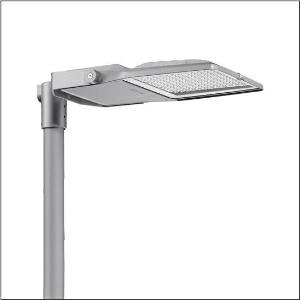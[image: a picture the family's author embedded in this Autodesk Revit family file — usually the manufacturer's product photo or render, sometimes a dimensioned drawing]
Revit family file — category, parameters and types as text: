
# Revit family: floodlight_fl_21_iq_midi___pl52_5xa7781f2d3a_fab9
name_source: partatom
category: Lighting Fixtures
units: mm (PartAtom-declared; Revit-internal decimal feet)

## family parameters
Cut with Voids When Loaded = No
Host = Face
Light Source = No
Part Type = Normal
Room Calculation Point = No
Round Connector Dimension = Use Diameter
Shared = No

## types (1)
- --- (1 x LED, 35760 lm, 270.2 W, 3000K)
    Apparent Load = 270 VA
    CIE Flux Codes = 26 60 98 100 100
    Color Rendering = 70
    Color Temperature = 3000K
    Default Elevation = 1800 mm
    Description = Floodlight FL 21 iQ midi, floodlight, primary light control with lens, of PMMA, primary optical cover: protective disc, of toughened safety glass, transparent, light distribution: PL52, light emission: direct distribution, installation type: surface-mounted, LED, High Power LED, rated luminous flux: 35.760lm, luminous efficacy: 132lm/W, light colour: 730, colour temperature: 3000K, control gear: ECG iQ, control: optimised constant luminous flux control (CLO 2.0), Desk-Remote (wireless, voltage-free reading and setting of iQ features in the workshop via application-optimized NFC function/RFID function), Light-Fading, Smart-Wire, Night-Set, Lumen-Switch, Temp-Guard, Auto-Match, with terminal, 6-pole, mains connection: 220..240V, AC, 50/60Hz, start of lifetime: 270W, end of service life: 287W, reduction: 117W, luminaire housing, of diecast aluminium, powder-coated, Siteco® metallic grey (DB 702S), corrosivity category C5 mid according to DIN EN ISO 12944, sealing non-destructively replaceable, please order mast flange separately, mast bracket, of steel, galvanised, powder-coated, Siteco® metallic grey (DB 702S), protection rating (complete): IP66, insulation class (complete): insulation class II (safety insulation), certification: CE, protection symbol: D, impact resistance: IK08, permissible operating ambient temperature: -40..+40°C, permissible operating ambient temperature for outdoor applications: -40..+50°C, standard: DIN EN 12944, LABS conformity tested according to VDMA 24364:2018-05, packaging unit: 1 piece

Light Distribution: PL52
    Height = 76 mm
    Lamp = 1 x LED
    Lamp Light Flux = 35760 lm
    Lamp Power = 270.2 W
    Lamp count = 1
    Length = 657 mm
    Luminous efficacy = 132 lm/W
    Manufacturer = Siteco
    ModVariant = No
    Model = 5XA7781F2D3A
    Number of Poles = 1
    OnlyDefault = Yes
    Power Factor = 1
    Product Name = Floodlight FL 21 iQ midi | PL52
    Product group = floodlight | pylon annexe
    ProductGroupID = 6200
    Protection Class = Protection class II
    Protection Degree = IP 66
    RLX_Detail_Level = 1
    RLX_Emergency_Light_Flux = 0 lm
    RLX_Emergency_Type = 0
    RLX_Emergency_Type_DB = No
    RlxData = <blob elided: 153797 chars, md5=249a4d37>
    Socket = socket
    Standby Power = 0 W
    System Light Flux = 35760 lm
    System Power = 270 W
    Type Comments = factory setting: luminous flux: 100 % | dim-lin: 254 | 620 mA
    Type Image = l_1007123.jpg
    URL = http://relux.com
    VarID = @adj_035953
    Voltage = 0 V
    Weight = 0.00 kg
    Width = 442 mm

## geometry (parser evidence)
native form markers: Blend x4, Sweep x15
no freeform markers — native parametric forms only
